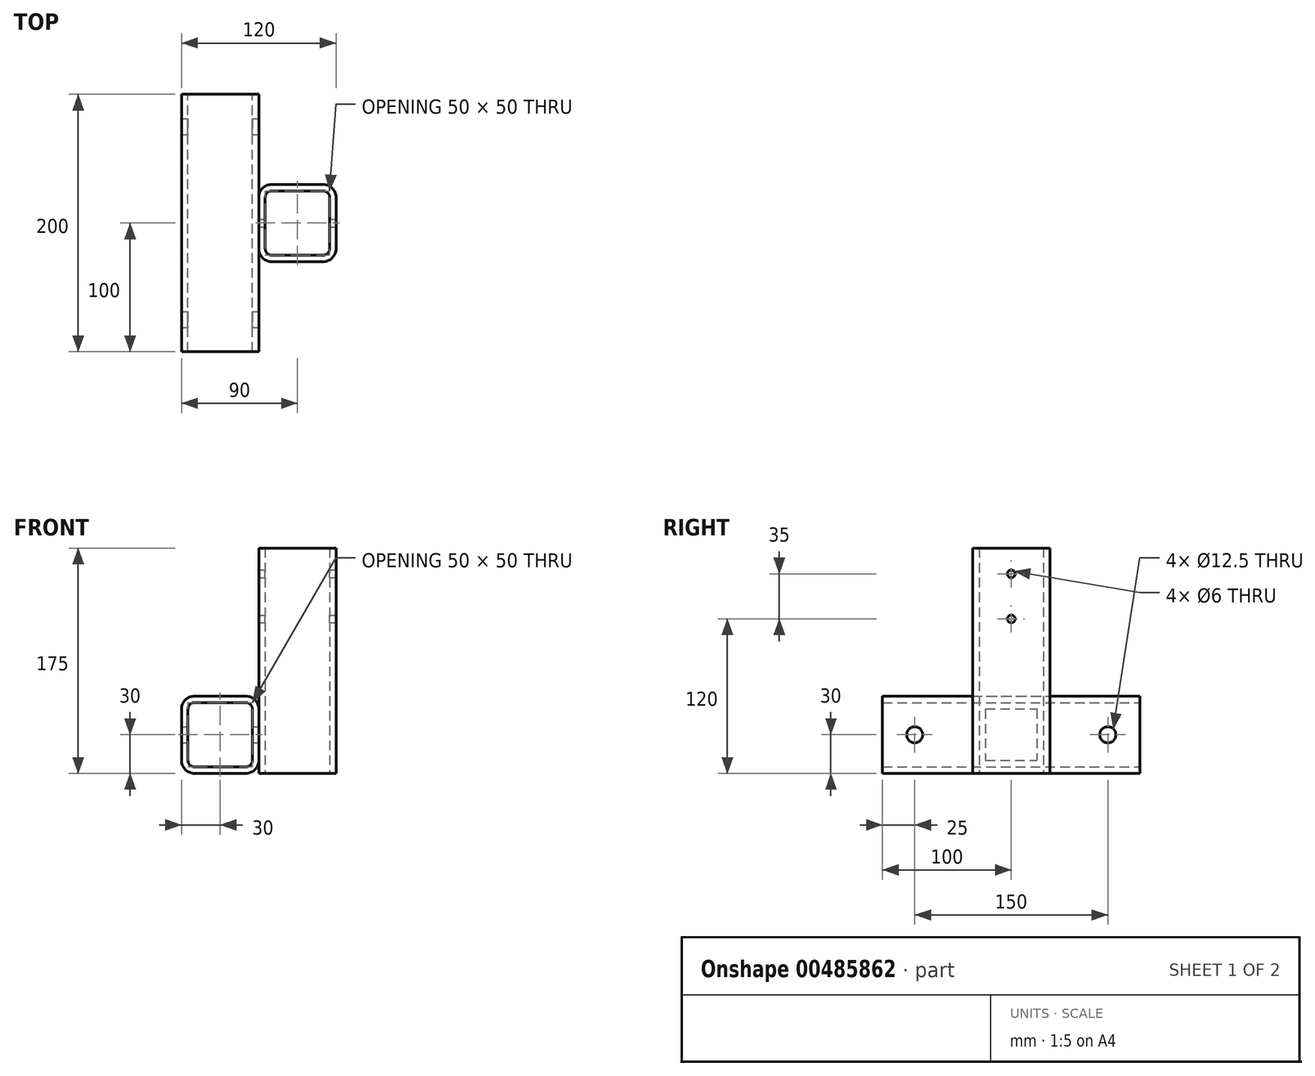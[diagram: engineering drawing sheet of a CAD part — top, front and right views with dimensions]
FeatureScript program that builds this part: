
annotation { "Feature Type Name" : "Feature", "Feature Type Description" : "" }
export const myFeature = defineFeature(function(context is Context, id is Id, definition is map)
    precondition{}
    {
        {
            var Q0;
            Q0=qCreatedBy(makeId("Top.planeOp"),FACE);
            var sketch = newSketch(context, id + "F0", { "sketchPlane" : qUnion([Q0])});
            skLineSegment(sketch, "E0.bottom", {"start": v(-20, 30) * mm, "end": v(20, 30) * mm});
            skLineSegment(sketch, "E0.top", {"start": v(-20, -30) * mm, "end": v(20, -30) * mm});
            skLineSegment(sketch, "E0.left", {"start": v(-30, 20) * mm, "end": v(-30, -20) * mm});
            skLineSegment(sketch, "E0.right", {"start": v(30, 20) * mm, "end": v(30, -20) * mm});
            skPoint(sketch, "E0.middle", {"position": v(0, 0) * mm});
            skPoint(sketch, "E1.visualSharp", {"position": v(-30, -30) * mm});
            skArc(sketch, "E1.filletArc", {"start": v(-30, -20) * mm, "mid": v(-27.07, -27.07) * mm, "end": v(-20, -30) * mm});
            skPoint(sketch, "E2.visualSharp", {"position": v(30, -30) * mm});
            skArc(sketch, "E2.filletArc", {"start": v(20, -30) * mm, "mid": v(27.07, -27.07) * mm, "end": v(30, -20) * mm});
            skPoint(sketch, "E3.visualSharp", {"position": v(30, 30) * mm});
            skArc(sketch, "E3.filletArc", {"start": v(30, 20) * mm, "mid": v(27.07, 27.07) * mm, "end": v(20, 30) * mm});
            skPoint(sketch, "E4.visualSharp", {"position": v(-30, 30) * mm});
            skArc(sketch, "E4.filletArc", {"start": v(-20, 30) * mm, "mid": v(-27.07, 27.07) * mm, "end": v(-30, 20) * mm});
            skArc(sketch, "E5.0", {"start": v(-20, 25) * mm, "mid": v(-23.54, 23.54) * mm, "end": v(-25, 20) * mm});
            skLineSegment(sketch, "E5.1", {"start": v(-20, 25) * mm, "end": v(20, 25) * mm});
            skLineSegment(sketch, "E5.2", {"start": v(-25, 20) * mm, "end": v(-25, -20) * mm});
            skArc(sketch, "E5.3", {"start": v(25, 20) * mm, "mid": v(23.54, 23.54) * mm, "end": v(20, 25) * mm});
            skArc(sketch, "E5.4", {"start": v(-25, -20) * mm, "mid": v(-23.54, -23.54) * mm, "end": v(-20, -25) * mm});
            skLineSegment(sketch, "E5.5", {"start": v(-20, -25) * mm, "end": v(20, -25) * mm});
            skArc(sketch, "E5.6", {"start": v(20, -25) * mm, "mid": v(23.54, -23.54) * mm, "end": v(25, -20) * mm});
            skLineSegment(sketch, "E5.7", {"start": v(25, 20) * mm, "end": v(25, -20) * mm});
            skSolve(sketch);
        }
        {
            var Q0;
            Q0=qSketchRegion(id+"F0",true);
            extrude(context, id + "F1", {"entities" : qUnion([Q0]), "endBound" : BoundingType.SYMMETRIC, "depth" : 175 * mm, "offsetDistance" : 25 * mm});
        }
        {
            var Q0;
            Q0=qCreatedBy(makeId("Front.planeOp"),FACE);
            var sketch = newSketch(context, id + "F2", { "sketchPlane" : qUnion([Q0])});
            skLineSegment(sketch, "E6.bottom", {"start": v(-80, -27.5) * mm, "end": v(-40, -27.5) * mm});
            skLineSegment(sketch, "E6.top", {"start": v(-80, -87.5) * mm, "end": v(-40, -87.5) * mm});
            skLineSegment(sketch, "E6.left", {"start": v(-90, -37.5) * mm, "end": v(-90, -77.5) * mm});
            skLineSegment(sketch, "E6.right", {"start": v(-30, -37.5) * mm, "end": v(-30, -77.5) * mm});
            skPoint(sketch, "E6.middle", {"position": v(-60, -57.5) * mm});
            skPoint(sketch, "E7.visualSharp", {"position": v(-30, -27.5) * mm});
            skArc(sketch, "E7.filletArc", {"start": v(-30, -37.5) * mm, "mid": v(-32.93, -30.43) * mm, "end": v(-40, -27.5) * mm});
            skPoint(sketch, "E8.visualSharp", {"position": v(-90, -27.5) * mm});
            skArc(sketch, "E8.filletArc", {"start": v(-80, -27.5) * mm, "mid": v(-87.07, -30.43) * mm, "end": v(-90, -37.5) * mm});
            skPoint(sketch, "E9.visualSharp", {"position": v(-90, -87.5) * mm});
            skArc(sketch, "E9.filletArc", {"start": v(-90, -77.5) * mm, "mid": v(-87.07, -84.57) * mm, "end": v(-80, -87.5) * mm});
            skPoint(sketch, "E10.visualSharp", {"position": v(-30, -87.5) * mm});
            skArc(sketch, "E10.filletArc", {"start": v(-40, -87.5) * mm, "mid": v(-32.93, -84.57) * mm, "end": v(-30, -77.5) * mm});
            skLineSegment(sketch, "E11.0", {"start": v(-35, -37.5) * mm, "end": v(-35, -77.5) * mm});
            skArc(sketch, "E11.1", {"start": v(-40, -82.5) * mm, "mid": v(-36.46, -81.04) * mm, "end": v(-35, -77.5) * mm});
            skArc(sketch, "E11.2", {"start": v(-35, -37.5) * mm, "mid": v(-36.46, -33.96) * mm, "end": v(-40, -32.5) * mm});
            skLineSegment(sketch, "E11.3", {"start": v(-80, -82.5) * mm, "end": v(-40, -82.5) * mm});
            skLineSegment(sketch, "E11.4", {"start": v(-80, -32.5) * mm, "end": v(-40, -32.5) * mm});
            skArc(sketch, "E11.5", {"start": v(-80, -32.5) * mm, "mid": v(-83.54, -33.96) * mm, "end": v(-85, -37.5) * mm});
            skLineSegment(sketch, "E11.6", {"start": v(-85, -37.5) * mm, "end": v(-85, -77.5) * mm});
            skArc(sketch, "E11.7", {"start": v(-85, -77.5) * mm, "mid": v(-83.54, -81.04) * mm, "end": v(-80, -82.5) * mm});
            skSolve(sketch);
        }
        {
            var Q0;
            Q0=qSketchRegion(id+"F2",true);
            extrude(context, id + "F3", {"entities" : qUnion([Q0]), "operationType" : NewBodyOperationType.ADD, "endBound" : BoundingType.SYMMETRIC, "depth" : 200 * mm, "offsetDistance" : 25 * mm});
        }
        {
            var Q0;
            {var subQ2=sQuery(id+"F2.wireOp",EDGE,"E6.right");Q0=makeQuery(id+"F3.boolean.opBoolean","SPLIT",FACE,{"disambiguationData":[TD([makeQuery(id+"F1.opExtrude","SWEPT_FACE",FACE,{"disambiguationData":[OSD([sQuery(id+"F0.wireOp",EDGE,"E4.filletArc")])]})])],"derivedFrom":makeQuery(id+"F3.opExtrude","SWEPT_FACE",FACE,{"disambiguationData":[OSD([subQ2])]})});}
            var sketch = newSketch(context, id + "F4", { "sketchPlane" : qUnion([Q0])});
            skCircle(sketch, "E12", {"center": v(-75, -57.5) * mm, "radius": 6.25 * mm});
            skLineSegment(sketch, "E13", {"start": v(0, 0) * mm, "end": v(0, -87.5) * mm, "construction": true});
            skCircle(sketch, "E14.MirrorC", {"center": v(75, -57.5) * mm, "radius": 6.25 * mm});
            skSolve(sketch);
        }
        {
            var Q0;
            Q0=qSketchRegion(id+"F4",true);
            extrude(context, id + "F5", {"entities" : qUnion([Q0]), "operationType" : NewBodyOperationType.REMOVE, "endBound" : BoundingType.THROUGH_ALL, "oppositeDirection" : true, "depth" : 25 * mm, "offsetDistance" : 25 * mm});
        }
        {
            var Q0;
            Q0=makeQuery(id+"F1.opExtrude","SWEPT_FACE",FACE,{"disambiguationData":[OSD([sQuery(id+"F0.wireOp",EDGE,"E0.right")])]});
            var sketch = newSketch(context, id + "F6", { "sketchPlane" : qUnion([Q0])});
            skCircle(sketch, "E15", {"center": v(0, 32.5) * mm, "radius": 3 * mm});
            skCircle(sketch, "E16.0.1.0", {"center": v(0, 67.5) * mm, "radius": 3 * mm});
            skLineSegment(sketch, "E16.direction1", {"start": v(0, 32.5) * mm, "end": v(25, 32.5) * mm, "construction": true});
            skLineSegment(sketch, "E16.direction2", {"start": v(0, 32.5) * mm, "end": v(0, 67.5) * mm, "construction": true});
            skSolve(sketch);
        }
        {
            var Q0;
            Q0=qSketchRegion(id+"F6",true);
            extrude(context, id + "F7", {"entities" : qUnion([Q0]), "operationType" : NewBodyOperationType.REMOVE, "endBound" : BoundingType.THROUGH_ALL, "oppositeDirection" : true, "depth" : 25 * mm, "offsetDistance" : 25 * mm});
        }
    });
